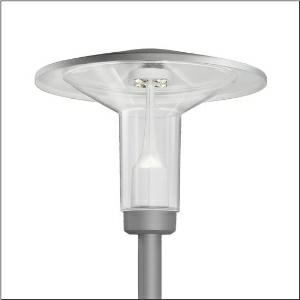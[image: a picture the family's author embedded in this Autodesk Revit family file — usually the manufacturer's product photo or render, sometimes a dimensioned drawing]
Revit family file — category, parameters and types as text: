
# Revit family: laterne___st1_2a_5xa5255ef14h_dffd
name_source: partatom
category: Lighting Fixtures
units: mm (PartAtom-declared; Revit-internal decimal feet)

## family parameters
Cut with Voids When Loaded = No
Host = Face
Light Source = No
Part Type = Normal
Room Calculation Point = No
Round Connector Dimension = Use Diameter
Shared = No

## types (1)
- --- (1 x LED, 1540 lm, 10.5 W, 3000K)
    Apparent Load = 11 VA
    CIE Flux Codes = 25 63 94 98 100
    Color Rendering = 70
    Color Temperature = 3000K
    Default Elevation = 1800 mm
    Description = Lantern, mast luminaire, Module 540 iQ-SR, primary light control with 3 zone facetted reflector, of plastic, silver coated, highly specular, structured, primary optical cover: cover, of PMMA, transparent, light distribution: ST1.2a, light emission: direct distribution, primary light characteristic: asymmetric, installation type: post-top, LED, High Power LED, rated luminous flux: 1.540lm, luminous efficacy: 147lm/W, light colour: 730, colour temperature: 3000K, control gear: ECG iQ, control: Auto-Match, Temp-Guard, Lumen-Switch, Night-Set, Smart-Wire, Light-Fading, Desk-Remote (wireless, voltage-free reading and setting of iQ features in the workshop via application-optimized NFC function/RFID function), optimised constant luminous flux control (CLO 2.0), Street-Remote, presetting dimming logarithmic, with terminal, 6-pole, max. 2.5mm², mains connection: 220..240V, AC, 50/60Hz, start of lifetime: 11W, end of lifetime: 11W, reduction: 5W, luminaire housing, upper part, of glass-fibre reinforced polyester, coated, Siteco® metallic grey (DB 702S), diameter: 750mm, height: 583mm, spigot size: d x l = 76 x 70mm (post-top) | with reducer (optional accessory) 60 x 70mm, post-top mast mounting element, of diecast aluminium, coated, Siteco® metallic grey (DB 702S), Module 540 iQ-SR, traffic white (RAL 9016), equipment: standard, protection rating (complete): IP65, insulation class (complete): insulation class II (safety insulation), certification: CE, ENEC, VDE, packaging unit: 1 piece

Light Distribution: ST1.2a
    Height = 583 mm
    Lamp = 1 x LED
    Lamp Light Flux = 1540 lm
    Lamp Power = 10.5 W
    Lamp count = 1
    Length = 750 mm
    Luminous efficacy = 147 lm/W
    Manufacturer = Siteco
    ModVariant = No
    Model = 5XA5255EF14H
    Number of Poles = 1
    OnlyDefault = Yes
    Power Factor = 1
    Product Name = Laterne | ST1.2a
    Product group = mast luminaire | pylon top
    ProductGroupID = 6100
    Protection Class = Protection class II
    Protection Degree = IP 65
    RLX_Detail_Level = 1
    RlxData = <blob elided: 103621 chars, md5=65f20626>
    Socket = socket
    Standby Power = 0 W
    System Light Flux = 1540 lm
    System Power = 11 W
    Type Comments = factory setting: luminous flux: 100 % | dim-lin: 254 | 419 mA
    Type Image = l_1006050.jpg
    URL = http://relux.com
    VarID = @adj_071881
    Voltage = 0 V
    Weight = 0.00 kg
    Width = 0 mm  [stored 0 ft]

note: [stored X ft] marks values corroborated as IEEE doubles in the binary element streams (Revit-internal decimal feet)

## geometry (parser evidence)
native form markers: Blend x4, Sweep x8
no freeform markers — native parametric forms only
